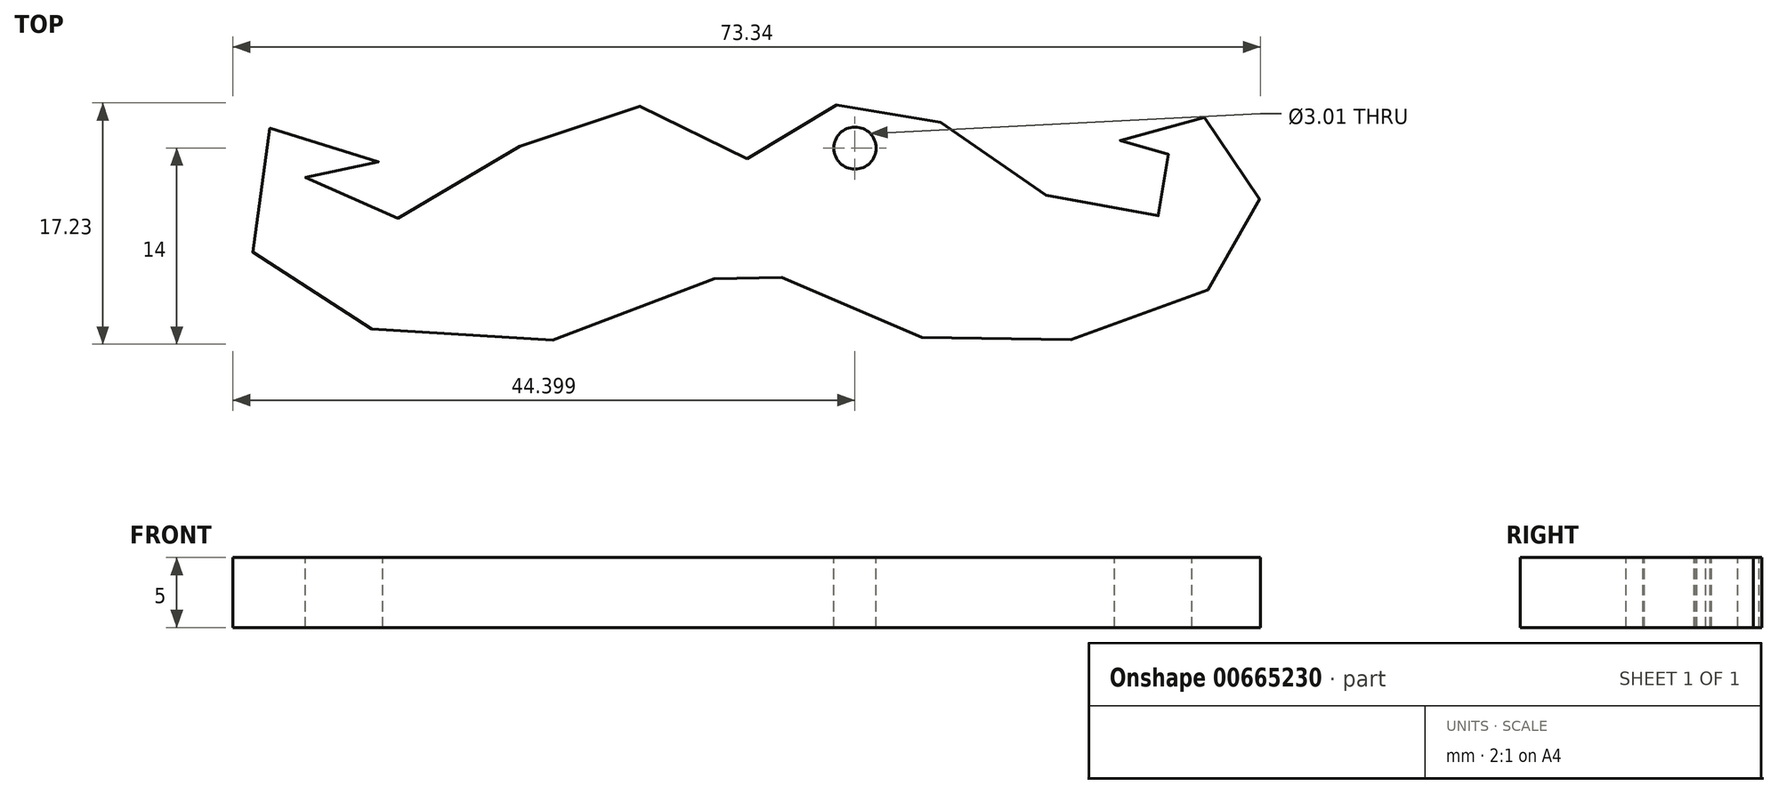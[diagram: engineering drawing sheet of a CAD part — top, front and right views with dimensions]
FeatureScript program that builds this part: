
annotation { "Feature Type Name" : "Feature", "Feature Type Description" : "" }
export const myFeature = defineFeature(function(context is Context, id is Id, definition is map)
    precondition{}
    {
        {
            var Q0;
            Q0=qCreatedBy(makeId("Top.planeOp"),FACE);
            var sketch = newSketch(context, id + "F0", { "sketchPlane" : qUnion([Q0])});
            skFitSpline(sketch, "E0", {"points": [v(-42.02, 22.15) * mm, v(-45.43, 24.98) * mm, v(-48.38, 25.8) * mm, v(-52.03, 25.92) * mm, v(-55.44, 24.86) * mm, v(-60.27, 21.56) * mm, v(-64.75, 18.85) * mm, v(-68.04, 17.67) * mm, v(-71.46, 18.38) * mm, v(-73.46, 20.26) * mm, v(-72.99, 21.91) * mm, v(-70.63, 22.38) * mm, v(-69.1, 21.32) * mm, v(-68.04, 23.2) * mm, v(-72.28, 25.56) * mm, v(-77.58, 22.86) * mm, v(-78.64, 18.5) * mm, v(-76.52, 14.5) * mm, v(-72.87, 11.67) * mm, v(-67.1, 9.55) * mm, v(-58.5, 8.96) * mm, v(-50.97, 10.25) * mm, v(-44.37, 13.55) * mm, v(-42.37, 16.26) * mm, v(-41.66, 16.38) * mm, v(-39.54, 13.67) * mm, v(-33.98, 10.58) * mm, v(-28.98, 9.27) * mm, v(-23.62, 8.9) * mm, v(-18, 9.34) * mm, v(-13.83, 10.33) * mm, v(-8.21, 13.58) * mm, v(-6.15, 16.82) * mm, v(-5.65, 17.88) * mm, v(-5.4, 19.88) * mm, v(-5.65, 21.87) * mm, v(-7.96, 24.3) * mm, v(-10.7, 25.5) * mm, v(-12.89, 25.18) * mm, v(-14.76, 24.06) * mm, v(-15.63, 23.06) * mm, v(-15.7, 22) * mm, v(-14.51, 21.5) * mm, v(-12.64, 22.37) * mm, v(-11.02, 22.12) * mm, v(-10.27, 20.75) * mm, v(-11.4, 18.94) * mm, v(-13.2, 17.88) * mm, v(-15.88, 17.88) * mm, v(-19.63, 19) * mm, v(-23.93, 21.75) * mm, v(-26.86, 24) * mm, v(-29.3, 25.18) * mm, v(-31.3, 25.74) * mm, v(-34.72, 26.12) * mm, v(-37.84, 25.24) * mm, v(-40.09, 23.68) * mm, v(-42.02, 22.15) * mm]});
            skSolve(sketch);
        }
        {
            var Q0;
            Q0=makeQuery(id+"F0.imprint","IMPRINT",FACE,{"disambiguationData":[TD([[makeQuery(id+"F0.imprint","IMPRINT",EDGE,{"derivedFrom":sQuery(id+"F0.wireOp",EDGE,"E0")}),1.0]])]});
            extrude(context, id + "F1", {"entities" : qUnion([Q0]), "oppositeDirection" : true, "depth" : 5 * mm, "offsetDistance" : 25.4 * mm});
        }
        {
            var Q0;
            Q0=qCreatedBy(makeId("Top.planeOp"),FACE);
            var sketch = newSketch(context, id + "F2", { "sketchPlane" : qUnion([Q0])});
            skCircle(sketch, "E1", {"center": v(-34.32, 22.9) * mm, "radius": 1.5 * mm});
            skSolve(sketch);
        }
        {
            var Q0;
            Q0=makeQuery(id+"F2.imprint","IMPRINT",FACE,{"disambiguationData":[TD([[makeQuery(id+"F2.imprint","IMPRINT",EDGE,{"derivedFrom":sQuery(id+"F2.wireOp",EDGE,"E1")}),1.0]])]});
            extrude(context, id + "F3", {"entities" : qUnion([Q0]), "operationType" : NewBodyOperationType.REMOVE, "oppositeDirection" : true, "depth" : 5 * mm, "offsetDistance" : 25.4 * mm});
        }
    });
